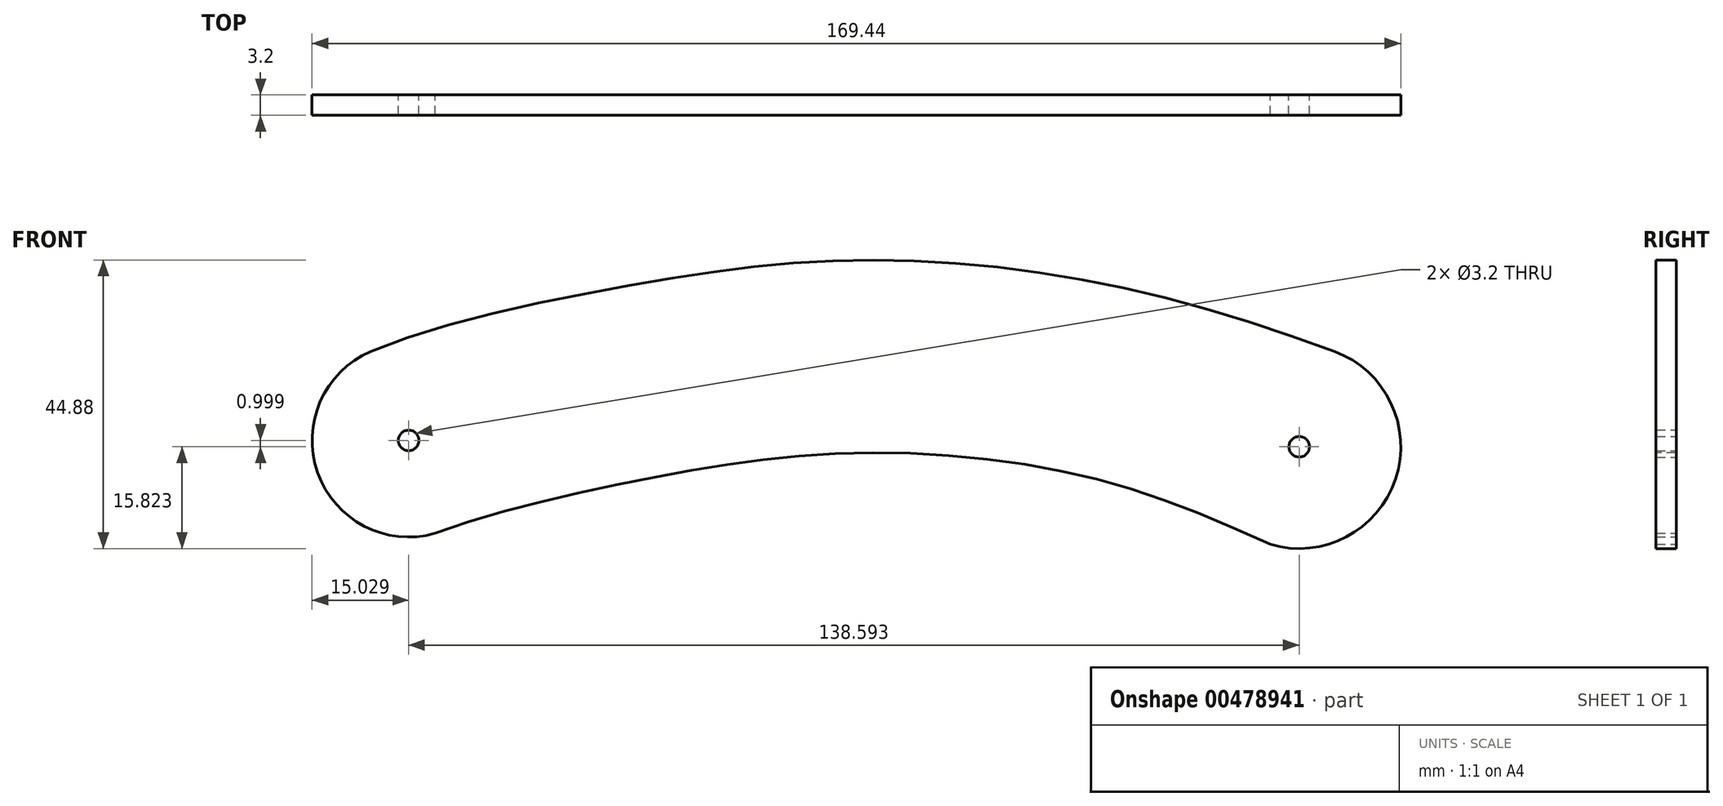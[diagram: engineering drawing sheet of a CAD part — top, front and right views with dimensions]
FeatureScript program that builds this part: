
annotation { "Feature Type Name" : "Feature", "Feature Type Description" : "" }
export const myFeature = defineFeature(function(context is Context, id is Id, definition is map)
    precondition{}
    {
        {
            var Q0;
            Q0=qCreatedBy(makeId("Front.planeOp"),FACE);
            var sketch = newSketch(context, id + "F0", { "sketchPlane" : qUnion([Q0])});
            skFitSpline(sketch, "E0", {"points": [v(75, 0) * mm, v(36.3, 11.07) * mm, v(0, 14.2) * mm, v(-34.84, 10.25) * mm, v(-75, 0) * mm], "startDerivative": vector(-156.8, 58.35) * mm, "endDerivative": vector(-121.03, -51.54) * mm});
            skFitSpline(sketch, "E1", {"points": [v(65, -30) * mm, v(34.06, -18.93) * mm, v(0, -15.8) * mm, v(-31.8, -19.75) * mm, v(-65, -28.28) * mm], "startDerivative": vector(-137.83, 62.94) * mm, "endDerivative": vector(-116.37, -42.93) * mm});
            skArc(sketch, "E2", {"start": v(-75, 0) * mm, "mid": v(-83.28, -18.84) * mm, "end": v(-65, -28.28) * mm});
            skArc(sketch, "E3", {"start": v(75, 0) * mm, "mid": v(84.5, -19.83) * mm, "end": v(65, -30) * mm});
            skCircle(sketch, "E4", {"center": v(69.48, -14.83) * mm, "radius": 1.6 * mm});
            skCircle(sketch, "E5", {"center": v(-69.11, -13.83) * mm, "radius": 1.6 * mm});
            skSolve(sketch);
        }
        {
            var Q0;
            Q0 = qSketchRegion(id + "F0", true);
            extrude(context, id + "F1", {"entities" : qUnion([Q0]), "depth" : 3.2 * mm, "offsetDistance" : 25 * mm});
        }
    });
